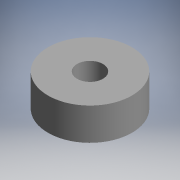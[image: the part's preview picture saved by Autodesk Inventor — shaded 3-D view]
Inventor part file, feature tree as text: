
AUTODESK INVENTOR PART (.ipt)
format: ipt  version: 2017 (Build 210142000, 142)  size: 74,752 bytes
history: native  units: mm (DEFAULTED — no unit token found)
features: extrude x1, sketch x1
ambient origin geometry x8: Origin, YZ Plane, XZ Plane, XY Plane, X Axis, Y Axis, Z Axis, Center Point
bodies: Solid1 (feature_tree)
feature tree (2):
  extrude  "Extrusion1"  [1 undecoded]
  sketch  "Sketch1"  dims[d3=0.0mm]
note: 1 required parameter value undecoded (feature->parameter linkage not recoverable at this tier; creation-order binding heuristic only, values carry confidence <= 0.55)
